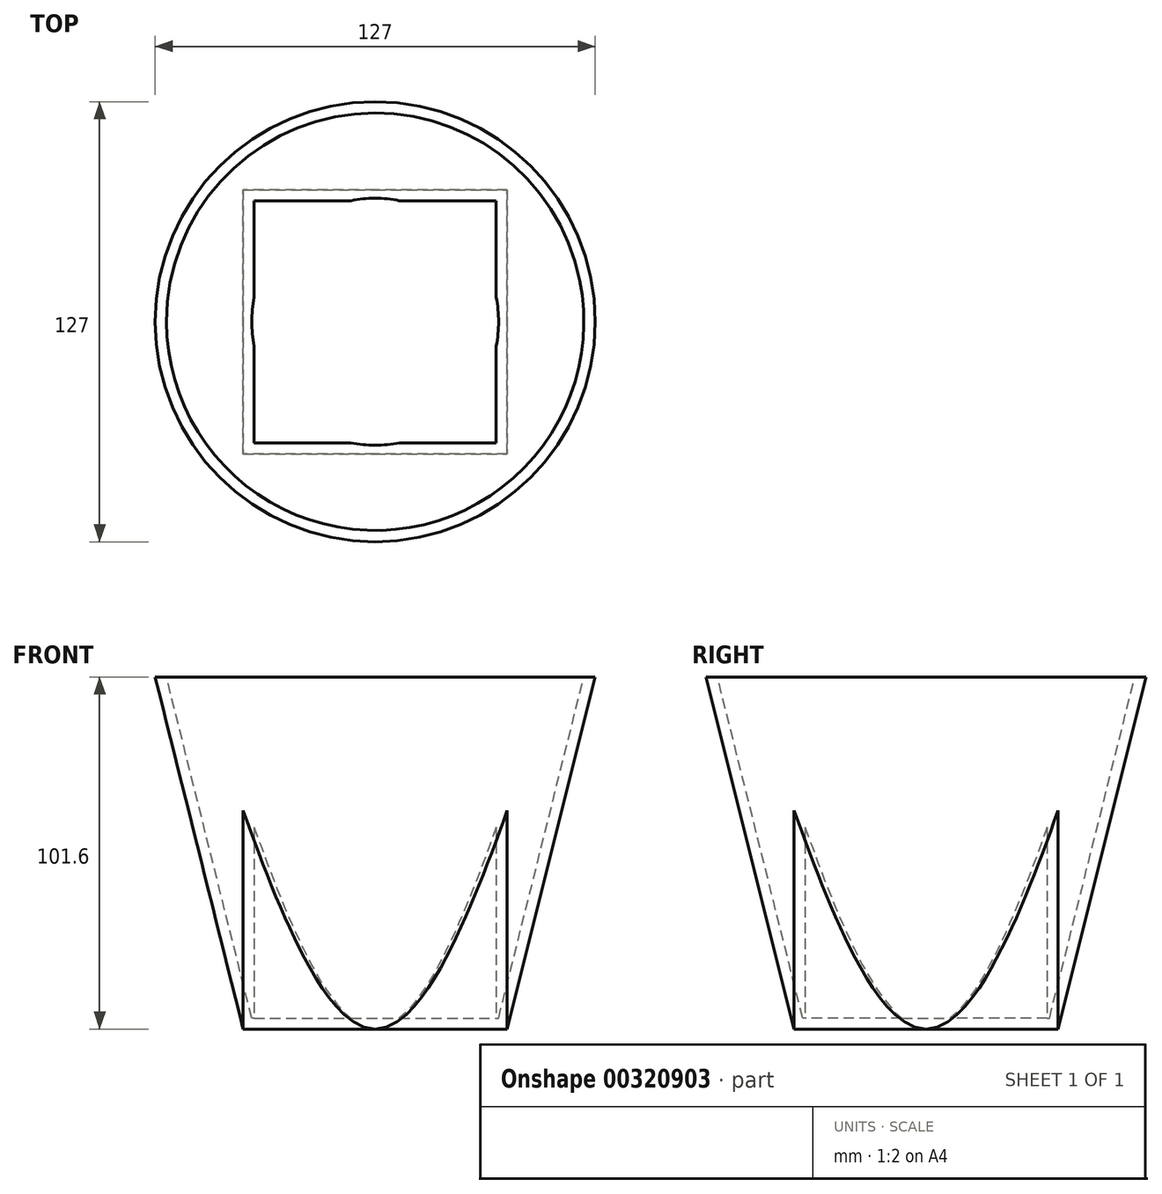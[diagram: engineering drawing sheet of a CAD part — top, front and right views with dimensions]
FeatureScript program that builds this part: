
annotation { "Feature Type Name" : "Feature", "Feature Type Description" : "" }
export const myFeature = defineFeature(function(context is Context, id is Id, definition is map)
    precondition{}
    {
        {
            var Q0;
            Q0=qCreatedBy(makeId("Front.planeOp"),FACE);
            var sketch = newSketch(context, id + "F0", { "sketchPlane" : qUnion([Q0])});
            skLineSegment(sketch, "E0", {"start": v(0, 0) * mm, "end": v(0, 101.6) * mm});
            skLineSegment(sketch, "E1", {"start": v(0, 0) * mm, "end": v(38.1, 0) * mm});
            skLineSegment(sketch, "E2", {"start": v(0, 101.6) * mm, "end": v(63.5, 101.6) * mm});
            skLineSegment(sketch, "E3", {"start": v(63.5, 101.6) * mm, "end": v(38.1, 0) * mm});
            skSolve(sketch);
        }
        {
            var Q0;
            Q0=makeQuery(id+"F0.imprint","IMPRINT",FACE,{"disambiguationData":[TD([[makeQuery(id+"F0.imprint","IMPRINT",EDGE,{"derivedFrom":sQuery(id+"F0.wireOp",EDGE,"E0")}),-1.0]])]});
            var Q1;
            Q1=sQuery(id+"F0.wireOp",EDGE,"E0");
            revolve(context, id + "F1", {"entities" : qUnion([Q0]), "axis" : qUnion([Q1]), "revolveType" : RevolveType.FULL});
        }
        {
            var Q0;
            Q0=makeQuery(id+"F1.opRevolve","SWEPT_FACE",FACE,{"disambiguationData":[OSD([sQuery(id+"F0.wireOp",EDGE,"E1")])]});
            var sketch = newSketch(context, id + "F2", { "sketchPlane" : qUnion([Q0])});
            skLineSegment(sketch, "E4.bottom", {"start": v(-38.1, 0) * mm, "end": v(38.1, 0) * mm});
            skLineSegment(sketch, "E4.top", {"start": v(-38.1, 38.1) * mm, "end": v(38.1, 38.1) * mm});
            skLineSegment(sketch, "E4.left", {"start": v(-38.1, 0) * mm, "end": v(-38.1, 38.1) * mm});
            skLineSegment(sketch, "E4.right", {"start": v(38.1, 0) * mm, "end": v(38.1, 38.1) * mm});
            skLineSegment(sketch, "E5.top", {"start": v(-38.1, -38.1) * mm, "end": v(38.1, -38.1) * mm});
            skLineSegment(sketch, "E5.left", {"start": v(-38.1, 0) * mm, "end": v(-38.1, -38.1) * mm});
            skLineSegment(sketch, "E5.right", {"start": v(38.1, 0) * mm, "end": v(38.1, -38.1) * mm});
            skSolve(sketch);
        }
        {
            var Q0;
            Q0 = qSketchRegion(id + "F2", true);
            extrude(context, id + "F3", {"entities" : qUnion([Q0]), "operationType" : NewBodyOperationType.ADD, "oppositeDirection" : true, "depth" : 101.6 * mm});
        }
        {
            var Q0;
            Q0=makeQuery(id+"F1.opRevolve","SWEPT_FACE",FACE,{"disambiguationData":[OSD([sQuery(id+"F0.wireOp",EDGE,"E2")])]});
            shell(context, id + "F4", {"entities" : qUnion([Q0]), "thickness" : 3.17 * mm});
        }
    });
